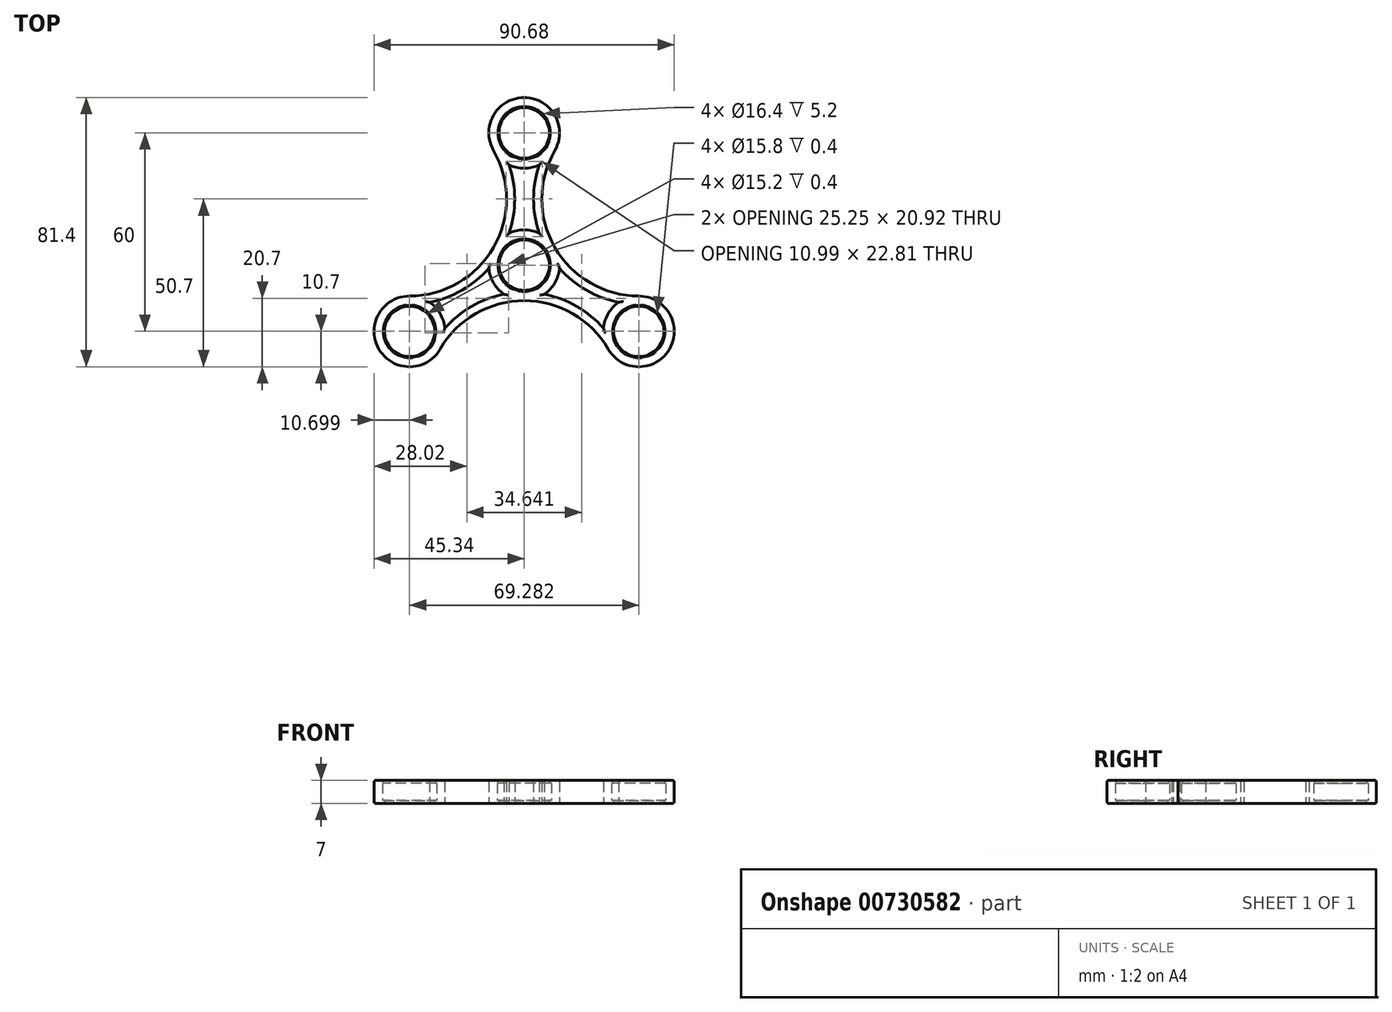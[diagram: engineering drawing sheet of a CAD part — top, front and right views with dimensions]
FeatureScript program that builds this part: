
annotation { "Feature Type Name" : "Feature", "Feature Type Description" : "" }
export const myFeature = defineFeature(function(context is Context, id is Id, definition is map)
    precondition{}
    {
        {
            var Q0;
            Q0=qCreatedBy(makeId("Top.planeOp"),FACE);
            var sketch = newSketch(context, id + "F0", { "sketchPlane" : qUnion([Q0])});
            skLineSegment(sketch, "E0", {"start": v(0, 40) * mm, "end": v(0, 0) * mm, "construction": true});
            skLineSegment(sketch, "E1", {"start": v(0, 0) * mm, "end": v(34.64, -20) * mm, "construction": true});
            skLineSegment(sketch, "E2", {"start": v(-34.64, -20) * mm, "end": v(0, 0) * mm, "construction": true});
            skCircle(sketch, "E3", {"center": v(0, 40) * mm, "radius": 8.2 * mm});
            skCircle(sketch, "E4", {"center": v(34.64, -20) * mm, "radius": 8.2 * mm});
            skCircle(sketch, "E5", {"center": v(-34.64, -20) * mm, "radius": 8.2 * mm});
            skCircle(sketch, "E6", {"center": v(0, 0) * mm, "radius": 8.2 * mm});
            skCircle(sketch, "E7", {"center": v(0, 0) * mm, "radius": 40 * mm, "construction": true});
            skArc(sketch, "E8", {"start": v(-23.98, -19.11) * mm, "mid": v(-25.37, -14.65) * mm, "end": v(-28.54, -11.2) * mm});
            skArc(sketch, "E9", {"start": v(6.1, -8.8) * mm, "mid": v(9.27, -5.35) * mm, "end": v(10.66, -0.89) * mm});
            skArc(sketch, "E10", {"start": v(25.37, -25.35) * mm, "mid": v(43.9, -25.35) * mm, "end": v(34.64, -9.3) * mm});
            skArc(sketch, "E11", {"start": v(9.27, 34.65) * mm, "mid": v(0, 50.7) * mm, "end": v(-9.27, 34.65) * mm});
            skArc(sketch, "E12", {"start": v(-23.98, -19.11) * mm, "mid": v(-15.9, -12.46) * mm, "end": v(-6.1, -8.8) * mm});
            skArc(sketch, "E13", {"start": v(-25.37, -25.35) * mm, "mid": v(0, -10.7) * mm, "end": v(25.37, -25.35) * mm});
            skArc(sketch, "E14", {"start": v(4.56, 30.32) * mm, "mid": v(2.84, 20) * mm, "end": v(4.56, 9.68) * mm});
            skArc(sketch, "E15", {"start": v(9.27, 34.65) * mm, "mid": v(9.27, 5.35) * mm, "end": v(34.64, -9.3) * mm});
            skArc(sketch, "E16", {"start": v(-4.56, 30.32) * mm, "mid": v(-2.84, 20) * mm, "end": v(-4.56, 9.68) * mm});
            skArc(sketch, "E17", {"start": v(-9.27, 34.65) * mm, "mid": v(-9.27, 5.35) * mm, "end": v(-34.64, -9.3) * mm});
            skArc(sketch, "E18.trimOffspring", {"start": v(-34.64, -9.3) * mm, "mid": v(-43.9, -25.35) * mm, "end": v(-25.37, -25.35) * mm});
            skArc(sketch, "E19.trimOffspring", {"start": v(6.1, -8.8) * mm, "mid": v(15.9, -12.46) * mm, "end": v(23.98, -19.11) * mm});
            skArc(sketch, "E20.trimOffspring", {"start": v(28.54, -11.2) * mm, "mid": v(25.37, -14.65) * mm, "end": v(23.98, -19.11) * mm});
            skArc(sketch, "E21.trimOffspring", {"start": v(4.56, 9.68) * mm, "mid": v(0, 10.7) * mm, "end": v(-4.56, 9.68) * mm});
            skArc(sketch, "E22.trimOffspring", {"start": v(10.66, -0.89) * mm, "mid": v(18.74, -7.54) * mm, "end": v(28.54, -11.2) * mm});
            skArc(sketch, "E23.trimOffspring", {"start": v(-10.66, -0.89) * mm, "mid": v(-18.74, -7.54) * mm, "end": v(-28.54, -11.2) * mm});
            skArc(sketch, "E24.trimOffspring", {"start": v(-10.66, -0.89) * mm, "mid": v(-9.27, -5.35) * mm, "end": v(-6.1, -8.8) * mm});
            skArc(sketch, "E25.trimOffspring", {"start": v(-4.56, 30.32) * mm, "mid": v(0, 29.3) * mm, "end": v(4.56, 30.32) * mm});
            skSolve(sketch);
        }
        {
            var Q0;
            Q0 = qSketchRegion(id + "F0", true);
            extrude(context, id + "F1", {"entities" : qUnion([Q0]), "depth" : 7 * mm, "offsetDistance" : 25 * mm});
        }
        {
            var Q0;
            Q0=makeQuery(id+"F1.opExtrude","CAP_FACE",FACE,{"disambiguationData":[OSD([sQuery(id+"F0.wireOp",EDGE,"E3"),sQuery(id+"F0.wireOp",EDGE,"E4"),sQuery(id+"F0.wireOp",EDGE,"E5"),sQuery(id+"F0.wireOp",EDGE,"E6"),sQuery(id+"F0.wireOp",EDGE,"E8"),sQuery(id+"F0.wireOp",EDGE,"E9"),sQuery(id+"F0.wireOp",EDGE,"E10"),sQuery(id+"F0.wireOp",EDGE,"E11"),sQuery(id+"F0.wireOp",EDGE,"E12"),sQuery(id+"F0.wireOp",EDGE,"E13"),sQuery(id+"F0.wireOp",EDGE,"E14"),sQuery(id+"F0.wireOp",EDGE,"E15"),sQuery(id+"F0.wireOp",EDGE,"E16"),sQuery(id+"F0.wireOp",EDGE,"E17"),sQuery(id+"F0.wireOp",EDGE,"E18.trimOffspring"),sQuery(id+"F0.wireOp",EDGE,"E19.trimOffspring"),sQuery(id+"F0.wireOp",EDGE,"E20.trimOffspring"),sQuery(id+"F0.wireOp",EDGE,"E21.trimOffspring"),sQuery(id+"F0.wireOp",EDGE,"E22.trimOffspring"),sQuery(id+"F0.wireOp",EDGE,"E23.trimOffspring"),sQuery(id+"F0.wireOp",EDGE,"E24.trimOffspring"),sQuery(id+"F0.wireOp",EDGE,"E25.trimOffspring")])],"isStart":false});
            var sketch = newSketch(context, id + "F2", { "sketchPlane" : qUnion([Q0])});
            skCircle(sketch, "E26", {"center": v(-34.64, -20) * mm, "radius": 8.2 * mm});
            skPoint(sketch, "E26.first.point", {"position": v(-38.46, -12.74) * mm});
            skPoint(sketch, "E26.second.point", {"position": v(-28.34, -25.25) * mm});
            skPoint(sketch, "E26.third.point", {"position": v(-38.13, -27.42) * mm});
            skCircle(sketch, "E27", {"center": v(0, 0) * mm, "radius": 8.2 * mm});
            skPoint(sketch, "E27.first.point", {"position": v(-2.01, 7.95) * mm});
            skPoint(sketch, "E27.second.point", {"position": v(6.54, -4.95) * mm});
            skPoint(sketch, "E27.third.point", {"position": v(-6.03, -5.55) * mm});
            skCircle(sketch, "E28", {"center": v(34.64, -20) * mm, "radius": 8.2 * mm});
            skPoint(sketch, "E28.first.point", {"position": v(30.33, -13.02) * mm});
            skPoint(sketch, "E28.second.point", {"position": v(42.67, -21.65) * mm});
            skPoint(sketch, "E28.third.point", {"position": v(29.84, -26.65) * mm});
            skCircle(sketch, "E29", {"center": v(0, 40) * mm, "radius": 8.2 * mm});
            skPoint(sketch, "E29.first.point", {"position": v(-6.53, 44.96) * mm});
            skPoint(sketch, "E29.second.point", {"position": v(6.1, 45.48) * mm});
            skPoint(sketch, "E29.third.point", {"position": v(1.24, 31.9) * mm});
            skCircle(sketch, "E30", {"center": v(0, 40) * mm, "radius": 7.9 * mm});
            skCircle(sketch, "E31", {"center": v(0, 0) * mm, "radius": 7.9 * mm});
            skCircle(sketch, "E32", {"center": v(34.64, -20) * mm, "radius": 7.9 * mm});
            skCircle(sketch, "E33", {"center": v(-34.64, -20) * mm, "radius": 7.9 * mm});
            skSolve(sketch);
        }
        {
            var Q0;
            Q0 = qSketchRegion(id + "F2", true);
            extrude(context, id + "F3", {"entities" : qUnion([Q0]), "operationType" : NewBodyOperationType.ADD, "oppositeDirection" : true, "depth" : 0.9 * mm, "offsetDistance" : 25 * mm});
        }
        {
            var Q0;
            Q0=makeQuery(id+"F3.boolean.opBoolean","MERGE",FACE,{"derivedFrom":[makeQuery(id+"F1.opExtrude","CAP_FACE",FACE,{"disambiguationData":[OSD([sQuery(id+"F0.wireOp",EDGE,"E3"),sQuery(id+"F0.wireOp",EDGE,"E4"),sQuery(id+"F0.wireOp",EDGE,"E5"),sQuery(id+"F0.wireOp",EDGE,"E6"),sQuery(id+"F0.wireOp",EDGE,"E8"),sQuery(id+"F0.wireOp",EDGE,"E9"),sQuery(id+"F0.wireOp",EDGE,"E10"),sQuery(id+"F0.wireOp",EDGE,"E11"),sQuery(id+"F0.wireOp",EDGE,"E12"),sQuery(id+"F0.wireOp",EDGE,"E13"),sQuery(id+"F0.wireOp",EDGE,"E14"),sQuery(id+"F0.wireOp",EDGE,"E15"),sQuery(id+"F0.wireOp",EDGE,"E16"),sQuery(id+"F0.wireOp",EDGE,"E17"),sQuery(id+"F0.wireOp",EDGE,"E18.trimOffspring"),sQuery(id+"F0.wireOp",EDGE,"E19.trimOffspring"),sQuery(id+"F0.wireOp",EDGE,"E20.trimOffspring"),sQuery(id+"F0.wireOp",EDGE,"E21.trimOffspring"),sQuery(id+"F0.wireOp",EDGE,"E22.trimOffspring"),sQuery(id+"F0.wireOp",EDGE,"E23.trimOffspring"),sQuery(id+"F0.wireOp",EDGE,"E24.trimOffspring"),sQuery(id+"F0.wireOp",EDGE,"E25.trimOffspring")])],"isStart":false}),makeQuery(id+"F3.opExtrude","CAP_FACE",FACE,{"disambiguationData":[OSD([sQuery(id+"F2.wireOp",EDGE,"E26"),sQuery(id+"F2.wireOp",EDGE,"E33")])],"isStart":true}),makeQuery(id+"F3.opExtrude","CAP_FACE",FACE,{"disambiguationData":[OSD([sQuery(id+"F2.wireOp",EDGE,"E27"),sQuery(id+"F2.wireOp",EDGE,"E31")])],"isStart":true}),makeQuery(id+"F3.opExtrude","CAP_FACE",FACE,{"disambiguationData":[OSD([sQuery(id+"F2.wireOp",EDGE,"E28"),sQuery(id+"F2.wireOp",EDGE,"E32")])],"isStart":true}),makeQuery(id+"F3.opExtrude","CAP_FACE",FACE,{"disambiguationData":[OSD([sQuery(id+"F2.wireOp",EDGE,"E29"),sQuery(id+"F2.wireOp",EDGE,"E30")])],"isStart":true})]});
            fillet(context, id + "F4", {"entities" : qUnion([Q0]), "radius" : 0.5 * mm, "tangentPropagation" : true, "allowEdgeOverflow" : false});
        }
        {
            var Q0;
            Q0=makeQuery(id+"F1.opExtrude","CAP_FACE",FACE,{"disambiguationData":[OSD([sQuery(id+"F0.wireOp",EDGE,"E3"),sQuery(id+"F0.wireOp",EDGE,"E4"),sQuery(id+"F0.wireOp",EDGE,"E5"),sQuery(id+"F0.wireOp",EDGE,"E6"),sQuery(id+"F0.wireOp",EDGE,"E8"),sQuery(id+"F0.wireOp",EDGE,"E9"),sQuery(id+"F0.wireOp",EDGE,"E10"),sQuery(id+"F0.wireOp",EDGE,"E11"),sQuery(id+"F0.wireOp",EDGE,"E12"),sQuery(id+"F0.wireOp",EDGE,"E13"),sQuery(id+"F0.wireOp",EDGE,"E14"),sQuery(id+"F0.wireOp",EDGE,"E15"),sQuery(id+"F0.wireOp",EDGE,"E16"),sQuery(id+"F0.wireOp",EDGE,"E17"),sQuery(id+"F0.wireOp",EDGE,"E18.trimOffspring"),sQuery(id+"F0.wireOp",EDGE,"E19.trimOffspring"),sQuery(id+"F0.wireOp",EDGE,"E20.trimOffspring"),sQuery(id+"F0.wireOp",EDGE,"E21.trimOffspring"),sQuery(id+"F0.wireOp",EDGE,"E22.trimOffspring"),sQuery(id+"F0.wireOp",EDGE,"E23.trimOffspring"),sQuery(id+"F0.wireOp",EDGE,"E24.trimOffspring"),sQuery(id+"F0.wireOp",EDGE,"E25.trimOffspring")])],"isStart":true});
            var sketch = newSketch(context, id + "F5", { "sketchPlane" : qUnion([Q0])});
            skCircle(sketch, "E34", {"center": v(-34.64, 20) * mm, "radius": 8.2 * mm});
            skPoint(sketch, "E34.first.point", {"position": v(-40.44, 25.8) * mm});
            skPoint(sketch, "E34.second.point", {"position": v(-26.59, 21.53) * mm});
            skPoint(sketch, "E34.third.point", {"position": v(-36.24, 11.96) * mm});
            skCircle(sketch, "E35", {"center": v(0, 0) * mm, "radius": 8.2 * mm});
            skPoint(sketch, "E35.first.point", {"position": v(-4.31, 6.97) * mm});
            skPoint(sketch, "E35.second.point", {"position": v(6.4, 5.12) * mm});
            skPoint(sketch, "E35.third.point", {"position": v(0.89, -8.15) * mm});
            skCircle(sketch, "E36", {"center": v(0, -40) * mm, "radius": 8.2 * mm});
            skPoint(sketch, "E36.first.point", {"position": v(-1.44, -31.93) * mm});
            skPoint(sketch, "E36.second.point", {"position": v(8.14, -41.01) * mm});
            skPoint(sketch, "E36.third.point", {"position": v(-4.85, -46.6) * mm});
            skCircle(sketch, "E37", {"center": v(34.64, 20) * mm, "radius": 8.2 * mm});
            skPoint(sketch, "E37.first.point", {"position": v(31.9, 27.73) * mm});
            skPoint(sketch, "E37.second.point", {"position": v(42.74, 21.28) * mm});
            skPoint(sketch, "E37.third.point", {"position": v(31.26, 12.53) * mm});
            skCircle(sketch, "E38", {"center": v(-34.64, 20) * mm, "radius": 7.6 * mm});
            skCircle(sketch, "E39", {"center": v(0, 0) * mm, "radius": 7.6 * mm});
            skCircle(sketch, "E40", {"center": v(34.64, 20) * mm, "radius": 7.6 * mm});
            skCircle(sketch, "E41", {"center": v(0, -40) * mm, "radius": 7.6 * mm});
            skSolve(sketch);
        }
        {
            var Q0;
            Q0 = qSketchRegion(id + "F5", true);
            extrude(context, id + "F6", {"entities" : qUnion([Q0]), "oppositeDirection" : true, "depth" : 0.9 * mm, "offsetDistance" : 25 * mm});
        }
        {
            var Q0;
            Q0=makeQuery(id+"F1.opExtrude","SWEPT_BODY",BODY,{"disambiguationData":[OSD([sQuery(id+"F0.wireOp",EDGE,"E3"),sQuery(id+"F0.wireOp",EDGE,"E4"),sQuery(id+"F0.wireOp",EDGE,"E5"),sQuery(id+"F0.wireOp",EDGE,"E6"),sQuery(id+"F0.wireOp",EDGE,"E8"),sQuery(id+"F0.wireOp",EDGE,"E9"),sQuery(id+"F0.wireOp",EDGE,"E10"),sQuery(id+"F0.wireOp",EDGE,"E11"),sQuery(id+"F0.wireOp",EDGE,"E12"),sQuery(id+"F0.wireOp",EDGE,"E13"),sQuery(id+"F0.wireOp",EDGE,"E14"),sQuery(id+"F0.wireOp",EDGE,"E15"),sQuery(id+"F0.wireOp",EDGE,"E16"),sQuery(id+"F0.wireOp",EDGE,"E17"),sQuery(id+"F0.wireOp",EDGE,"E18.trimOffspring"),sQuery(id+"F0.wireOp",EDGE,"E19.trimOffspring"),sQuery(id+"F0.wireOp",EDGE,"E20.trimOffspring"),sQuery(id+"F0.wireOp",EDGE,"E21.trimOffspring"),sQuery(id+"F0.wireOp",EDGE,"E22.trimOffspring"),sQuery(id+"F0.wireOp",EDGE,"E23.trimOffspring"),sQuery(id+"F0.wireOp",EDGE,"E24.trimOffspring"),sQuery(id+"F0.wireOp",EDGE,"E25.trimOffspring")])]});
            var Q1;
            Q1=makeQuery(id+"F6.opExtrude","SWEPT_BODY",BODY,{"disambiguationData":[OSD([sQuery(id+"F5.wireOp",EDGE,"E34"),sQuery(id+"F5.wireOp",EDGE,"E38")])]});
            var Q2;
            Q2=makeQuery(id+"F6.opExtrude","SWEPT_BODY",BODY,{"disambiguationData":[OSD([sQuery(id+"F5.wireOp",EDGE,"E35"),sQuery(id+"F5.wireOp",EDGE,"E39")])]});
            var Q3;
            Q3=makeQuery(id+"F6.opExtrude","SWEPT_BODY",BODY,{"disambiguationData":[OSD([sQuery(id+"F5.wireOp",EDGE,"E36"),sQuery(id+"F5.wireOp",EDGE,"E41")])]});
            var Q4;
            Q4=makeQuery(id+"F6.opExtrude","SWEPT_BODY",BODY,{"disambiguationData":[OSD([sQuery(id+"F5.wireOp",EDGE,"E37"),sQuery(id+"F5.wireOp",EDGE,"E40")])]});
            booleanBodies(context, id + "F7", {"operationType" : BooleanOperationType.UNION, "tools" : qUnion([Q0, Q1, Q2, Q3, Q4])});
        }
        {
            var Q0;
            Q0=makeQuery(id+"F7.opBoolean","MERGE",FACE,{"derivedFrom":[makeQuery(id+"F1.opExtrude","CAP_FACE",FACE,{"disambiguationData":[OSD([sQuery(id+"F0.wireOp",EDGE,"E3"),sQuery(id+"F0.wireOp",EDGE,"E4"),sQuery(id+"F0.wireOp",EDGE,"E5"),sQuery(id+"F0.wireOp",EDGE,"E6"),sQuery(id+"F0.wireOp",EDGE,"E8"),sQuery(id+"F0.wireOp",EDGE,"E9"),sQuery(id+"F0.wireOp",EDGE,"E10"),sQuery(id+"F0.wireOp",EDGE,"E11"),sQuery(id+"F0.wireOp",EDGE,"E12"),sQuery(id+"F0.wireOp",EDGE,"E13"),sQuery(id+"F0.wireOp",EDGE,"E14"),sQuery(id+"F0.wireOp",EDGE,"E15"),sQuery(id+"F0.wireOp",EDGE,"E16"),sQuery(id+"F0.wireOp",EDGE,"E17"),sQuery(id+"F0.wireOp",EDGE,"E18.trimOffspring"),sQuery(id+"F0.wireOp",EDGE,"E19.trimOffspring"),sQuery(id+"F0.wireOp",EDGE,"E20.trimOffspring"),sQuery(id+"F0.wireOp",EDGE,"E21.trimOffspring"),sQuery(id+"F0.wireOp",EDGE,"E22.trimOffspring"),sQuery(id+"F0.wireOp",EDGE,"E23.trimOffspring"),sQuery(id+"F0.wireOp",EDGE,"E24.trimOffspring"),sQuery(id+"F0.wireOp",EDGE,"E25.trimOffspring")])],"isStart":true}),makeQuery(id+"F6.opExtrude","CAP_FACE",FACE,{"disambiguationData":[OSD([sQuery(id+"F5.wireOp",EDGE,"E34"),sQuery(id+"F5.wireOp",EDGE,"E38")])],"isStart":true}),makeQuery(id+"F6.opExtrude","CAP_FACE",FACE,{"disambiguationData":[OSD([sQuery(id+"F5.wireOp",EDGE,"E35"),sQuery(id+"F5.wireOp",EDGE,"E39")])],"isStart":true}),makeQuery(id+"F6.opExtrude","CAP_FACE",FACE,{"disambiguationData":[OSD([sQuery(id+"F5.wireOp",EDGE,"E36"),sQuery(id+"F5.wireOp",EDGE,"E41")])],"isStart":true}),makeQuery(id+"F6.opExtrude","CAP_FACE",FACE,{"disambiguationData":[OSD([sQuery(id+"F5.wireOp",EDGE,"E37"),sQuery(id+"F5.wireOp",EDGE,"E40")])],"isStart":true})]});
            fillet(context, id + "F8", {"entities" : qUnion([Q0]), "radius" : 0.5 * mm, "tangentPropagation" : true, "allowEdgeOverflow" : false});
        }
    });
